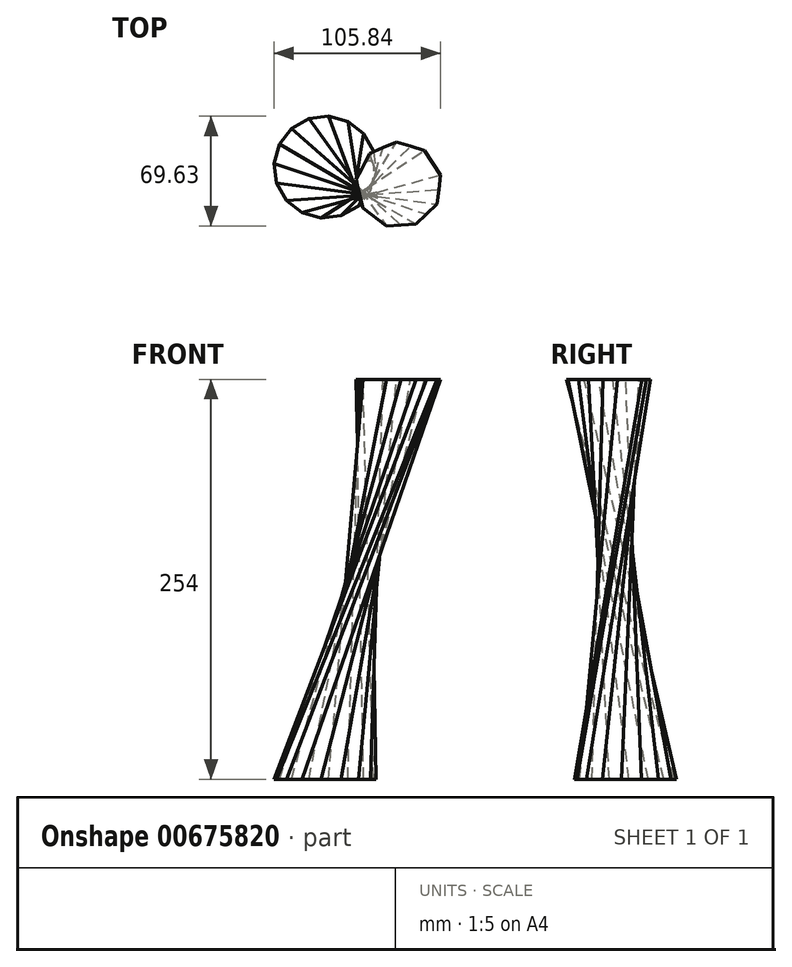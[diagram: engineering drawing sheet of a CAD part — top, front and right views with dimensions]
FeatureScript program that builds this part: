
annotation { "Feature Type Name" : "Feature", "Feature Type Description" : "" }
export const myFeature = defineFeature(function(context is Context, id is Id, definition is map)
    precondition{}
    {
        {
            var Q0;
            Q0=qCreatedBy(makeId("Top.planeOp"),FACE);
            var sketch = newSketch(context, id + "F0", { "sketchPlane" : qUnion([Q0])});
            skCircle(sketch, "E0.cCircle", {"center": v(-24.1, 17.08) * mm, "radius": 31.8 * mm, "construction": true});
            skLineSegment(sketch, "E0.0", {"start": v(8.25, 14.71) * mm, "end": v(4.89, 2.52) * mm});
            skLineSegment(sketch, "E0.1", {"start": v(4.89, 2.52) * mm, "end": v(-2.9, -7.46) * mm});
            skLineSegment(sketch, "E0.2", {"start": v(-2.9, -7.46) * mm, "end": v(-13.9, -13.7) * mm});
            skLineSegment(sketch, "E0.3", {"start": v(-13.9, -13.7) * mm, "end": v(-26.46, -15.26) * mm});
            skLineSegment(sketch, "E0.4", {"start": v(-26.46, -15.26) * mm, "end": v(-38.66, -11.9) * mm});
            skLineSegment(sketch, "E0.5", {"start": v(-38.66, -11.9) * mm, "end": v(-48.64, -4.11) * mm});
            skLineSegment(sketch, "E0.6", {"start": v(-48.64, -4.11) * mm, "end": v(-54.88, 6.9) * mm});
            skLineSegment(sketch, "E0.7", {"start": v(-54.88, 6.9) * mm, "end": v(-56.44, 19.45) * mm});
            skLineSegment(sketch, "E0.8", {"start": v(-56.44, 19.45) * mm, "end": v(-53.07, 31.65) * mm});
            skLineSegment(sketch, "E0.9", {"start": v(-53.07, 31.65) * mm, "end": v(-45.29, 41.63) * mm});
            skLineSegment(sketch, "E0.10", {"start": v(-45.29, 41.63) * mm, "end": v(-34.28, 47.87) * mm});
            skLineSegment(sketch, "E0.11", {"start": v(-34.28, 47.87) * mm, "end": v(-21.72, 49.43) * mm});
            skLineSegment(sketch, "E0.12", {"start": v(-21.72, 49.43) * mm, "end": v(-9.52, 46.06) * mm});
            skLineSegment(sketch, "E0.13", {"start": v(-9.52, 46.06) * mm, "end": v(0.46, 38.28) * mm});
            skLineSegment(sketch, "E0.14", {"start": v(0.46, 38.28) * mm, "end": v(6.7, 27.27) * mm});
            skLineSegment(sketch, "E0.15", {"start": v(6.7, 27.27) * mm, "end": v(8.25, 14.71) * mm});
            skPoint(sketch, "E0.0.midPoint", {"position": v(6.57, 8.61) * mm});
            skSolve(sketch);
        }
        {
            var Q0;
            Q0=qCreatedBy(makeId("Top.planeOp"),FACE);
            cPlane(context, id + "F1", {"entities" : qUnion([Q0]), "cplaneType" : CPlaneType.OFFSET, "offset" : 254 * mm, "width" : 152.4 * mm, "height" : 152.4 * mm});
        }
        {
            var Q0;
            Q0=qCreatedBy(id+"F1.planeOp",FACE);
            var sketch = newSketch(context, id + "F2", { "sketchPlane" : qUnion([Q0])});
            skCircle(sketch, "E1.cCircle", {"center": v(22.86, 5.9) * mm, "radius": 25.61 * mm, "construction": true});
            skLineSegment(sketch, "E1.0", {"start": v(-4.2, 9.12) * mm, "end": v(4.2, 25.76) * mm});
            skLineSegment(sketch, "E1.1", {"start": v(4.2, 25.76) * mm, "end": v(21.34, 33.1) * mm});
            skLineSegment(sketch, "E1.2", {"start": v(21.34, 33.1) * mm, "end": v(39.19, 27.72) * mm});
            skLineSegment(sketch, "E1.3", {"start": v(39.19, 27.72) * mm, "end": v(49.4, 12.12) * mm});
            skLineSegment(sketch, "E1.4", {"start": v(49.4, 12.12) * mm, "end": v(47.2, -6.4) * mm});
            skLineSegment(sketch, "E1.5", {"start": v(47.2, -6.4) * mm, "end": v(33.6, -19.16) * mm});
            skLineSegment(sketch, "E1.6", {"start": v(33.6, -19.16) * mm, "end": v(14.99, -20.2) * mm});
            skLineSegment(sketch, "E1.7", {"start": v(14.99, -20.2) * mm, "end": v(0.06, -9.03) * mm});
            skLineSegment(sketch, "E1.8", {"start": v(0.06, -9.03) * mm, "end": v(-4.2, 9.12) * mm});
            skPoint(sketch, "E1.0.midPoint", {"position": v(0, 17.44) * mm});
            skSolve(sketch);
        }
        {
            var Q0;
            Q0=makeQuery(id+"F0.imprint","IMPRINT",FACE,{"disambiguationData":[TD([[makeQuery(id+"F0.imprint","IMPRINT",EDGE,{"derivedFrom":sQuery(id+"F0.wireOp",EDGE,"E0.0")}),-1.0]])]});
            var Q1;
            Q1=makeQuery(id+"F2.imprint","IMPRINT",FACE,{"disambiguationData":[TD([[makeQuery(id+"F2.imprint","IMPRINT",EDGE,{"derivedFrom":sQuery(id+"F2.wireOp",EDGE,"E1.0")}),-1.0]])]});
            loft(context, id + "F3", {"sheetProfilesArray" : [{ "sheetProfileEntities" : qUnion([Q0]) }, { "sheetProfileEntities" : qUnion([Q1]) }]});
        }
    });
